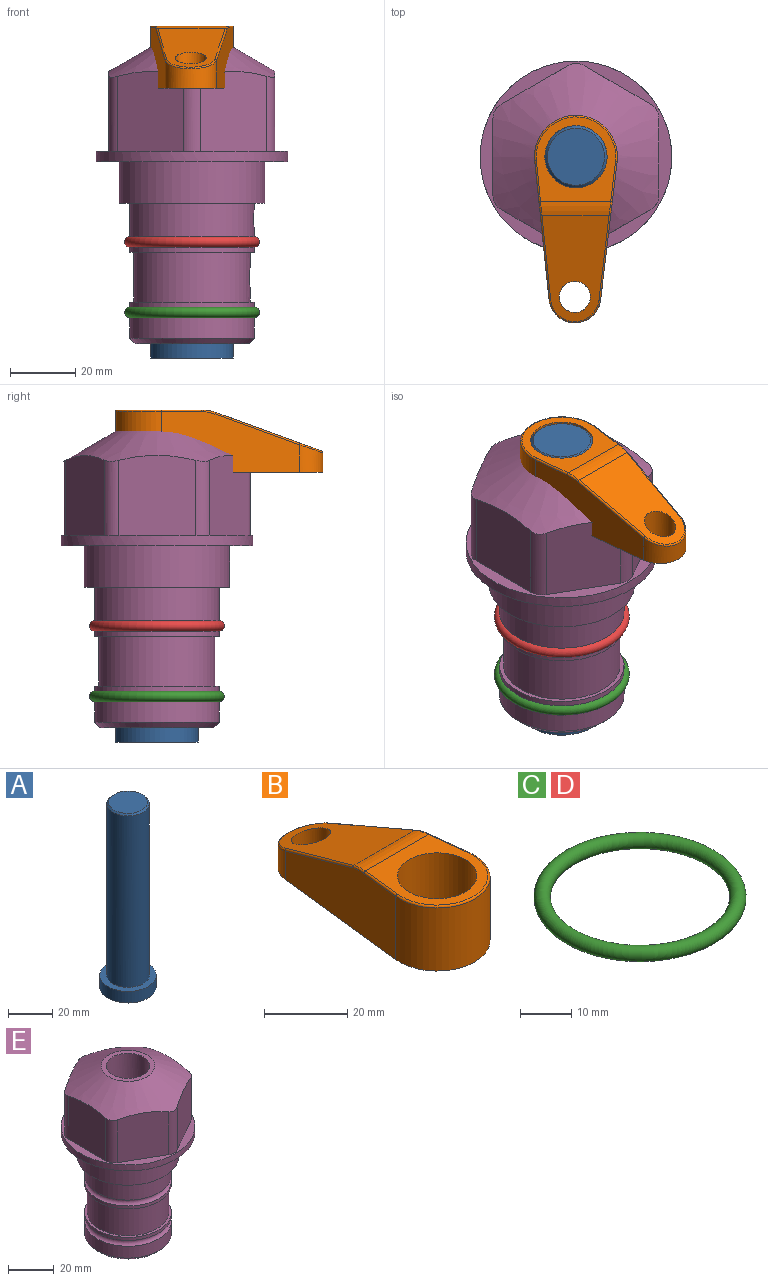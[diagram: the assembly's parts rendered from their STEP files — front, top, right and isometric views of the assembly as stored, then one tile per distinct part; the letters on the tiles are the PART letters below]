
ASSEMBLY  parts=5 mates=3
PART A: 6 faces, bbox 25.4x25.4x101.6 mm
  f0: plane 17.46x17.46mm, normal (0,0,1), area 239.5mm2, adj f5
  f1: plane 25.4x25.4mm, normal (0,0,-1), area 506.7mm2, adj f2
  f2: cylinder r=12.7mm len=25.4mm, axis (0,0,1), area 506.7mm2, adj f1,f3
  f3: plane 25.4x25.4mm, normal (0,0,1), area 221.7mm2, adj f2,f4
  f4: cylinder r=9.53mm len=94.46mm, axis (0,0,1), area 5653mm2, adj f3,f5
  f5: cone r=8.73mm half-angle=45deg, axis (0,0,-1), area 64.4mm2, adj f0,f4
PART B: 44 faces, bbox 27.5x64.5x19.1 mm
  f0: plane 2.3x0.95mm, normal (0,0,-1), area 1mm2, adj f25,f30,f34
  f1: plane 63.5x25.4mm, normal (0,0,-1), area 561.7mm2, adj f2,f3,f4,f5,f6,f7,f19,f20
  f2: cylinder r=12.7mm len=25.4mm, axis (0,0,-1), area 792.2mm2, adj f1,f3,f5,f13
  f3: plane 42.33x18.54mm, normal (0.99,0.11,0), area 647mm2, adj f1,f2,f4,f11,f12,f14
  f4: cylinder r=7.94mm len=15.78mm, axis (0,0,-1), area 158.6mm2, adj f1,f3,f5,f16
  f5: plane 42.33x18.54mm, normal (-0.99,0.11,0), area 647mm2, adj f1,f2,f4,f15,f17,f18
  f6: cylinder r=9.53mm len=19.05mm, axis (0,0,-1), area 1140.1mm2, adj f1,f8
  f7: cylinder r=4.76mm len=10.98mm, axis (0,0,-1), area 276.1mm2, adj f1,f9
  f8: plane 25.83x24.38mm, normal (0,0,1), area 262.2mm2, adj f6,f10,f11,f13,f15
  f9: plane 32.49x20.55mm, normal (0,0.34,0.94), area 489.9mm2, adj f7,f10,f14,f16,f18
  f10: cylinder r=12.7mm len=21.49mm, axis (-1,0,0), area 93.2mm2, adj f8,f9,f12,f17
  f11: cylinder r=0.51mm len=12.34mm, axis (0.11,-0.99,0), area 9.9mm2, adj f3,f8,f12,f13
  f12: bspline ~7.62x1.64mm, area 3.5mm2, adj f3,f10,f11,f14
  f13: torus R=12.19mm, axis (0,0,1), area 33.6mm2, adj f2,f8,f11,f15
  f14: cylinder r=0.51mm len=26.01mm, axis (0.1,-0.93,0.34), area 21.6mm2, adj f3,f9,f12,f16
  f15: cylinder r=0.51mm len=12.34mm, axis (0.11,0.99,0), area 9.9mm2, adj f5,f8,f13,f17
  f16: bspline ~15.78x7.05mm, area 15.7mm2, adj f4,f9,f14,f18
  f17: bspline ~7.62x1.64mm, area 3.5mm2, adj f5,f10,f15,f18
  f18: cylinder r=0.51mm len=26.01mm, axis (0.1,0.93,-0.34), area 21.6mm2, adj f5,f9,f16,f17
  f19: plane 21.6x14.29mm, normal (-0.99,-0.11,0), area 242.6mm2, adj f1,f26,f28,f34,f36,f38
  f20: plane 21.6x14.29mm, normal (0.99,-0.11,0), area 242.6mm2, adj f1,f27,f29,f37,f39,f41
  f21: cylinder r=12.7mm len=14.29mm, axis (0,0,-1), area 173.2mm2, adj f1,f26,f27,f30,f31,f33
  f22: cylinder r=7.94mm len=7.63mm, axis (0,0,-1), area 53.8mm2, adj f1,f28,f29,f42
  f23: plane 2.3x0.95mm, normal (0,0,-1), area 1mm2, adj f25,f33,f37
  f24: plane 17.94x12.32mm, normal (0,-0.34,-0.94), area 191.2mm2, adj f25,f38,f41,f42
  f25: cylinder r=9.53mm len=12.93mm, axis (-1,0,0), area 37.5mm2, adj f0,f23,f24,f31,f36,f39
  f26: cylinder r=1.59mm len=14.29mm, axis (0,0,-1), area 49mm2, adj f1,f19,f21,f32
  f27: cylinder r=1.59mm len=14.29mm, axis (0,0,-1), area 49mm2, adj f1,f20,f21,f35
  f28: cylinder r=1.59mm len=7.28mm, axis (0,0,-1), area 22.1mm2, adj f1,f19,f22,f40
  f29: cylinder r=1.59mm len=7.28mm, axis (0,0,-1), area 22.1mm2, adj f1,f20,f22,f43
  f30: torus R=14.29mm, axis (0,0,1), area 5.8mm2, adj f0,f21,f31,f32
  f31: bspline ~11.06x2.73mm, area 20.8mm2, adj f21,f25,f30,f33
  f32: sphere r=1.59mm, area 5.4mm2, adj f26,f30,f34
  f33: torus R=14.29mm, axis (0,0,1), area 5.8mm2, adj f21,f23,f31,f35
  f34: cylinder r=1.59mm len=1.68mm, axis (-0.11,0.99,0), area 2.4mm2, adj f0,f19,f32,f36
  f35: sphere r=1.59mm, area 5.4mm2, adj f27,f33,f37
  f36: bspline ~5.82x2.33mm, area 7.7mm2, adj f19,f25,f34,f38
  f37: cylinder r=1.59mm len=1.68mm, axis (0.11,0.99,0), area 2.4mm2, adj f20,f23,f35,f39
  f38: cylinder r=1.59mm len=18.33mm, axis (0.1,-0.93,0.34), area 46.7mm2, adj f19,f24,f36,f40
  f39: bspline ~5.82x2.33mm, area 7.7mm2, adj f20,f25,f37,f41
  f40: sphere r=1.59mm, area 3.6mm2, adj f28,f38,f42
  f41: cylinder r=1.59mm len=18.33mm, axis (0.1,0.93,-0.34), area 46.7mm2, adj f20,f24,f39,f43
  f42: bspline ~8.31x1.84mm, area 15.3mm2, adj f22,f24,f40,f43
  f43: sphere r=1.59mm, area 3.6mm2, adj f29,f41,f42
PART C: 1 faces, bbox 44.7x44.7x3.2 mm
  f0: torus R=19.05mm, axis (0,0,1), area 1193.9mm2
PART D: same geometry as C
PART E: 36 faces, bbox 58.7x58.7x91.2 mm
  f0: cylinder r=17.78mm len=35.56mm, axis (0,0,1), area 1670.8mm2, adj f23,f24,f31
  f1: cylinder r=19.05mm len=38.1mm, axis (0,0,1), area 1191.9mm2, adj f26,f27,f30
  f2: plane 58.66x58.66mm, normal (0,0,-1), area 1150.6mm2, adj f3,f28
  f3: cylinder r=29.33mm len=58.66mm, axis (0,0,-1), area 585.1mm2, adj f2,f4
  f4: plane 58.66x58.66mm, normal (0,0,1), area 475.9mm2, adj f3,f5,f6,f7,f8,f9,f10,f11
  f5: plane 24.5x20.32mm, normal (-0.5,0.87,0), area 562.8mm2, adj f4,f15,f16,f17
  f6: plane 24.5x20.32mm, normal (0.5,0.87,0), area 562.8mm2, adj f4,f14,f15,f17
  f7: plane 24.5x23.48mm, normal (1,0,0), area 562.8mm2, adj f4,f13,f14,f17
  f8: plane 24.5x20.32mm, normal (0.5,-0.87,0), area 562.8mm2, adj f4,f12,f13,f17
  f9: plane 24.5x20.32mm, normal (-0.5,-0.87,0), area 562.8mm2, adj f4,f11,f12,f17
  f10: plane 24.5x23.48mm, normal (-1,0,0), area 562.8mm2, adj f4,f11,f16,f17
  f11: cylinder r=5.08mm len=23.01mm, axis (0,0,-1), area 121.2mm2, adj f4,f9,f10,f17
  f12: cylinder r=5.08mm len=23.01mm, axis (0,0,-1), area 121.2mm2, adj f4,f8,f9,f17
  f13: cylinder r=5.08mm len=23.01mm, axis (0,0,-1), area 121.2mm2, adj f4,f7,f8,f17
  f14: cylinder r=5.08mm len=23.01mm, axis (0,0,-1), area 121.2mm2, adj f4,f6,f7,f17
  f15: cylinder r=5.08mm len=23.01mm, axis (0,0,-1), area 121.2mm2, adj f4,f5,f6,f17
  f16: cylinder r=5.08mm len=23.01mm, axis (0,0,-1), area 121.2mm2, adj f4,f5,f10,f17
  f17: cone r=11.73mm half-angle=60deg, axis (0,0,-1), area 2071.8mm2, adj f5,f6,f7,f8,f9,f10,f11,f12
  f18: plane 23.46x23.46mm, normal (0,0,1), area 147.4mm2, adj f17,f35
  f19: plane 34.93x34.93mm, normal (0,0,-1), area 958mm2, adj f29
  f20: cylinder r=19.05mm len=38.1mm, axis (0,0,1), area 760.1mm2, adj f21,f29
  f21: torus R=19.05mm, axis (0,0,1), area 565.3mm2, adj f20,f22
  f22: cylinder r=19.05mm len=38.1mm, axis (0,0,1), area 190mm2, adj f21,f23
  f23: plane 38.1x38.1mm, normal (0,0,1), area 146.9mm2, adj f0,f22
  f24: plane 38.1x38.1mm, normal (0,0,-1), area 146.9mm2, adj f0,f25
  f25: cylinder r=19.05mm len=38.1mm, axis (0,0,1), area 190mm2, adj f24,f26
  f26: torus R=19.05mm, axis (0,0,1), area 565.3mm2, adj f1,f25
  f27: plane 44.45x44.45mm, normal (0,0,-1), area 411.7mm2, adj f1,f28
  f28: cylinder r=22.23mm len=44.45mm, axis (0,0,1), area 1773.5mm2, adj f2,f27
  f29: cone r=19.05mm half-angle=45deg, axis (0,0,1), area 257.5mm2, adj f19,f20
  f30: cylinder r=3.17mm len=6.75mm, axis (-1,0,0), area 128mm2, adj f1,f33
  f31: cylinder r=3.17mm len=6.35mm, axis (-1,0,0), area 102.5mm2, adj f0,f33
  f32: plane 25.4x25.4mm, normal (0,0,1), area 506.7mm2, adj f33
  f33: cylinder r=12.7mm len=66.42mm, axis (0,0,-1), area 5236.2mm2, adj f30,f31,f32,f34
  f34: cone r=9.53mm half-angle=30deg, axis (0,0,-1), area 443.4mm2, adj f33,f35
  f35: cylinder r=9.53mm len=19.05mm, axis (0,0,-1), area 849mm2, adj f18,f34
PLACE A rot(axis=(0,0,-1),90.5deg) t=(0,0,-32.1)mm
PLACE B rot(axis=(0,0,1),179.5deg) t=(0,0,22.51)mm
PLACE C t=(0,0,-21.59)mm
PLACE D at identity
PLACE E at identity fixed
MATE fastened C.f0 <-> E.f0  axis (0,0,1) through (0,0,-46.1)mm
MATE cylindrical A.f2 <-> E.f0  axis (0,0,1) through (0,0,-6.46)mm
MATE fastened B.f2 <-> A.f2  axis (0,0,1) through (0,0,41.56)mm
